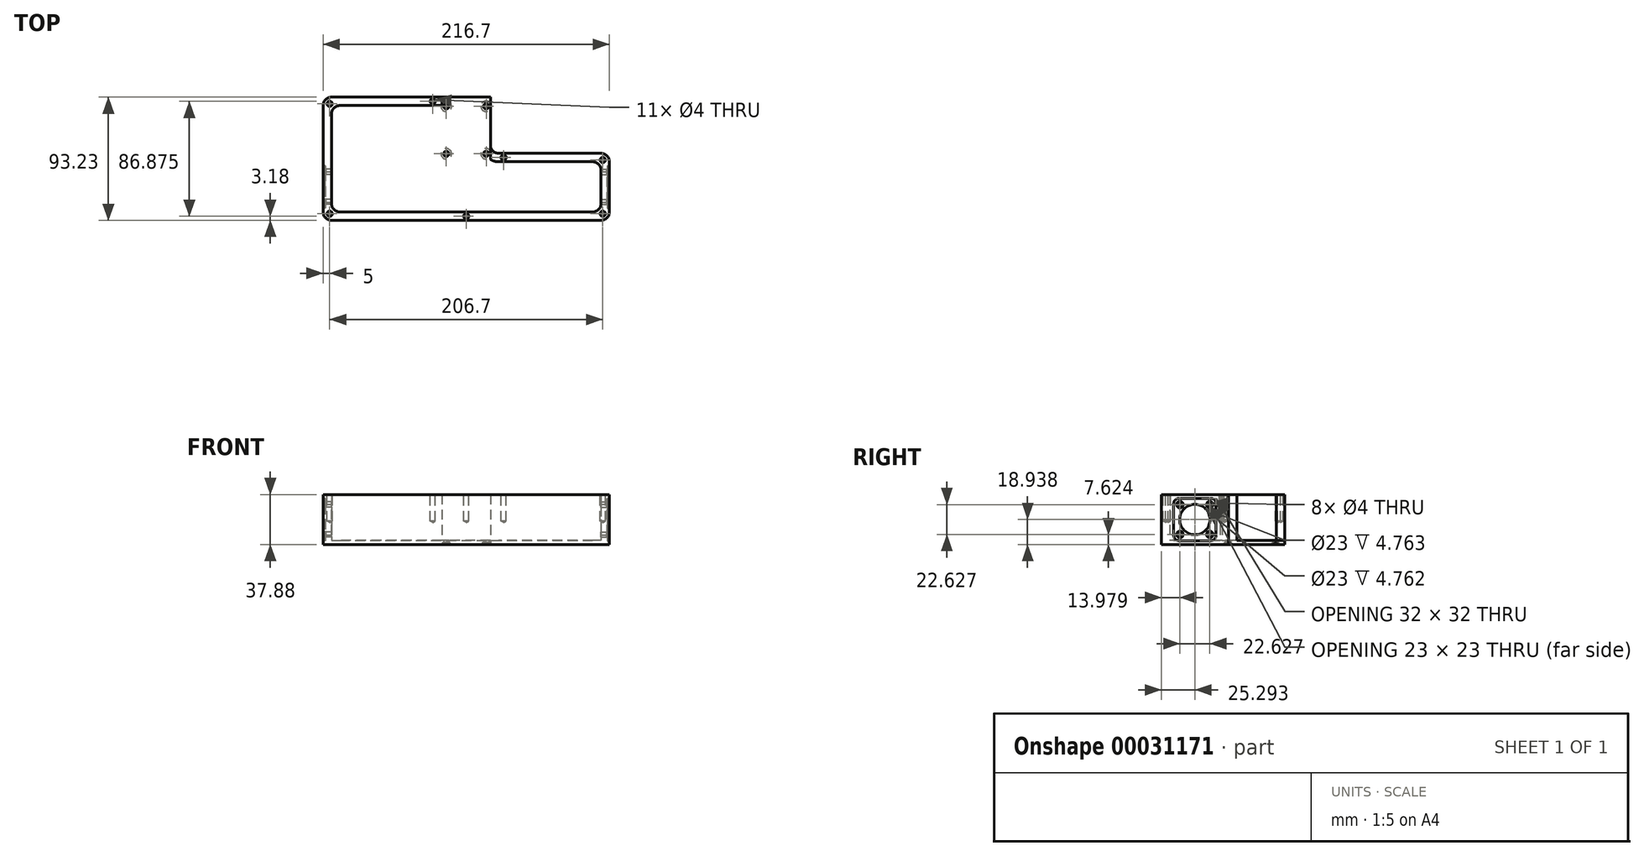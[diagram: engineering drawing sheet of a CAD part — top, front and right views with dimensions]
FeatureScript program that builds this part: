
annotation { "Feature Type Name" : "Feature", "Feature Type Description" : "" }
export const myFeature = defineFeature(function(context is Context, id is Id, definition is map)
    precondition{}
    {
        {
            var Q0;
            Q0=qCreatedBy(makeId("Top.planeOp"),FACE);
            var sketch = newSketch(context, id + "F0", { "sketchPlane" : qUnion([Q0])});
            skLineSegment(sketch, "E0", {"start": v(0, 0) * mm, "end": v(0, -93.23) * mm});
            skLineSegment(sketch, "E1", {"start": v(0, -93.23) * mm, "end": v(216.7, -93.23) * mm});
            skLineSegment(sketch, "E2", {"start": v(216.7, -93.23) * mm, "end": v(216.7, -42.52) * mm});
            skLineSegment(sketch, "E3", {"start": v(216.7, -42.52) * mm, "end": v(126.61, -42.52) * mm});
            skLineSegment(sketch, "E4", {"start": v(126.61, -42.52) * mm, "end": v(126.61, 0) * mm});
            skLineSegment(sketch, "E5", {"start": v(126.61, 0) * mm, "end": v(90.09, 0) * mm});
            skLineSegment(sketch, "E6", {"start": v(90.09, 0) * mm, "end": v(90.09, -93.23) * mm, "construction": true});
            skLineSegment(sketch, "E7", {"start": v(90.09, 0) * mm, "end": v(0, 0) * mm});
            skSolve(sketch);
        }
        {
            var Q0;
            Q0 = qSketchRegion(id + "F0", true);
            extrude(context, id + "F1", {"entities" : qUnion([Q0]), "depth" : 3.17 * mm});
        }
        {
            var Q0;
            Q0=makeQuery(id+"F1.opExtrude","SWEPT_EDGE",EDGE,{"disambiguationData":[OSD([sQuery(id+"F0.wireOp",EDGE,"E3"),sQuery(id+"F0.wireOp",EDGE,"E4")])]});
            fillet(context, id + "F2", {"entities" : qUnion([Q0]), "radius" : 6.35 * mm, "tangentPropagation" : true, "allowEdgeOverflow" : false});
        }
        {
            var Q0;
            Q0=makeQuery(id+"F1.opExtrude","SWEPT_EDGE",EDGE,{"disambiguationData":[OSD([sQuery(id+"F0.wireOp",EDGE,"E2"),sQuery(id+"F0.wireOp",EDGE,"E3")])]});
            var Q1;
            Q1=makeQuery(id+"F1.opExtrude","SWEPT_EDGE",EDGE,{"disambiguationData":[OSD([sQuery(id+"F0.wireOp",EDGE,"E1"),sQuery(id+"F0.wireOp",EDGE,"E2")])]});
            var Q2;
            Q2=makeQuery(id+"F1.opExtrude","SWEPT_EDGE",EDGE,{"disambiguationData":[OSD([sQuery(id+"F0.wireOp",EDGE,"E0"),sQuery(id+"F0.wireOp",EDGE,"E1")])]});
            var Q3;
            Q3=makeQuery(id+"F1.opExtrude","SWEPT_EDGE",EDGE,{"disambiguationData":[OSD([sQuery(id+"F0.wireOp",EDGE,"E0"),sQuery(id+"F0.wireOp",EDGE,"E7")])]});
            fillet(context, id + "F3", {"entities" : qUnion([Q0, Q1, Q2, Q3]), "radius" : 6.35 * mm, "tangentPropagation" : true, "allowEdgeOverflow" : false});
        }
        {
            var Q0;
            Q0=makeQuery(id+"F1.opExtrude","CAP_FACE",FACE,{"disambiguationData":[OSD([sQuery(id+"F0.wireOp",EDGE,"E0"),sQuery(id+"F0.wireOp",EDGE,"E1"),sQuery(id+"F0.wireOp",EDGE,"E2"),sQuery(id+"F0.wireOp",EDGE,"E3"),sQuery(id+"F0.wireOp",EDGE,"E4"),sQuery(id+"F0.wireOp",EDGE,"E5"),sQuery(id+"F0.wireOp",EDGE,"E7")])],"isStart":false});
            var sketch = newSketch(context, id + "F4", { "sketchPlane" : qUnion([Q0])});
            skArc(sketch, "E8.0", {"start": v(132.96, -48.88) * mm, "mid": v(129.68, -48.44) * mm, "end": v(126.61, -47.17) * mm});
            skLineSegment(sketch, "E8.1", {"start": v(204, -48.88) * mm, "end": v(132.96, -48.88) * mm});
            skLineSegment(sketch, "E8.2", {"start": v(90.09, -6.35) * mm, "end": v(12.7, -6.35) * mm});
            skLineSegment(sketch, "E8.3", {"start": v(6.35, -12.7) * mm, "end": v(6.35, -80.53) * mm});
            skLineSegment(sketch, "E8.4", {"start": v(12.7, -86.88) * mm, "end": v(204, -86.88) * mm});
            skLineSegment(sketch, "E8.5", {"start": v(210.35, -80.53) * mm, "end": v(210.35, -55.23) * mm});
            skPoint(sketch, "E9.visualSharp", {"position": v(6.35, -6.35) * mm});
            skArc(sketch, "E9.filletArc", {"start": v(12.7, -6.35) * mm, "mid": v(8.2, -8.2) * mm, "end": v(6.35, -12.7) * mm});
            skPoint(sketch, "E10.visualSharp", {"position": v(6.35, -86.88) * mm});
            skArc(sketch, "E10.filletArc", {"start": v(6.35, -80.53) * mm, "mid": v(8.2, -85.02) * mm, "end": v(12.7, -86.88) * mm});
            skPoint(sketch, "E11.visualSharp", {"position": v(210.35, -86.88) * mm});
            skArc(sketch, "E11.filletArc", {"start": v(204, -86.88) * mm, "mid": v(208.5, -85.02) * mm, "end": v(210.35, -80.53) * mm});
            skPoint(sketch, "E12.visualSharp", {"position": v(210.35, -48.88) * mm});
            skArc(sketch, "E12.filletArc", {"start": v(210.35, -55.23) * mm, "mid": v(208.5, -50.73) * mm, "end": v(204, -48.88) * mm});
            skLineSegment(sketch, "E13", {"start": v(90.09, -6.35) * mm, "end": v(90.09, 0) * mm});
            skLineSegment(sketch, "E14", {"start": v(126.61, -47.17) * mm, "end": v(126.61, -36.17) * mm});
            skLineSegment(sketch, "E15", {"start": v(90.09, 0) * mm, "end": v(6.35, 0) * mm});
            skLineSegment(sketch, "E16", {"start": v(0, -6.35) * mm, "end": v(0, -86.88) * mm});
            skLineSegment(sketch, "E17", {"start": v(6.35, -93.23) * mm, "end": v(210.35, -93.23) * mm});
            skLineSegment(sketch, "E18", {"start": v(216.7, -86.88) * mm, "end": v(216.7, -48.88) * mm});
            skLineSegment(sketch, "E19", {"start": v(210.35, -42.52) * mm, "end": v(132.96, -42.53) * mm});
            skArc(sketch, "E20", {"start": v(6.35, 0) * mm, "mid": v(1.86, -1.86) * mm, "end": v(0, -6.35) * mm});
            skArc(sketch, "E21", {"start": v(0, -86.88) * mm, "mid": v(1.86, -91.37) * mm, "end": v(6.35, -93.23) * mm});
            skArc(sketch, "E22", {"start": v(210.35, -93.22) * mm, "mid": v(214.84, -91.37) * mm, "end": v(216.7, -86.88) * mm});
            skArc(sketch, "E23", {"start": v(216.7, -48.88) * mm, "mid": v(214.84, -44.38) * mm, "end": v(210.35, -42.52) * mm});
            skArc(sketch, "E24", {"start": v(126.61, -36.17) * mm, "mid": v(128.47, -40.67) * mm, "end": v(132.96, -42.53) * mm});
            skSolve(sketch);
        }
        {
            var Q0;
            Q0 = qSketchRegion(id + "F4", true);
            extrude(context, id + "F5", {"entities" : qUnion([Q0]), "operationType" : NewBodyOperationType.ADD, "depth" : 34.7 * mm});
        }
        {
            var Q0;
            Q0=makeQuery(id+"F5.boolean.opBoolean","MERGE",FACE,{"derivedFrom":[makeQuery(id+"F1.opExtrude","SWEPT_FACE",FACE,{"disambiguationData":[OSD([sQuery(id+"F0.wireOp",EDGE,"E2")])]}),makeQuery(id+"F5.opExtrude","SWEPT_FACE",FACE,{"disambiguationData":[OSD([sQuery(id+"F4.wireOp",EDGE,"E18")])]})]});
            var sketch = newSketch(context, id + "F6", { "sketchPlane" : qUnion([Q0])});
            skLineSegment(sketch, "E25.rect.bottom", {"start": v(-55.94, 34.94) * mm, "end": v(-79.94, 34.94) * mm});
            skLineSegment(sketch, "E25.rect.top", {"start": v(-55.94, 2.94) * mm, "end": v(-79.94, 2.94) * mm});
            skLineSegment(sketch, "E25.rect.left", {"start": v(-51.94, 30.94) * mm, "end": v(-51.94, 6.94) * mm});
            skLineSegment(sketch, "E25.rect.right", {"start": v(-83.94, 30.94) * mm, "end": v(-83.94, 6.94) * mm});
            skPoint(sketch, "E25.rect.middle", {"position": v(-67.94, 18.94) * mm});
            skLineSegment(sketch, "E26", {"start": v(-83.94, 34.94) * mm, "end": v(-86.88, 34.94) * mm, "construction": true});
            skLineSegment(sketch, "E27", {"start": v(-83.94, 34.94) * mm, "end": v(-83.94, 37.88) * mm, "construction": true});
            skLineSegment(sketch, "E28", {"start": v(-83.94, 2.94) * mm, "end": v(-83.94, 0) * mm, "construction": true});
            skPoint(sketch, "E29.visualSharp", {"position": v(-83.94, 34.94) * mm});
            skArc(sketch, "E29.filletArc", {"start": v(-79.94, 34.94) * mm, "mid": v(-82.77, 33.77) * mm, "end": v(-83.94, 30.94) * mm});
            skPoint(sketch, "E30.visualSharp", {"position": v(-51.94, 34.94) * mm});
            skArc(sketch, "E30.filletArc", {"start": v(-51.94, 30.94) * mm, "mid": v(-53.1, 33.77) * mm, "end": v(-55.94, 34.94) * mm});
            skPoint(sketch, "E31.visualSharp", {"position": v(-51.94, 2.94) * mm});
            skArc(sketch, "E31.filletArc", {"start": v(-55.94, 2.94) * mm, "mid": v(-53.1, 4.1) * mm, "end": v(-51.94, 6.94) * mm});
            skPoint(sketch, "E32.visualSharp", {"position": v(-83.94, 2.94) * mm});
            skArc(sketch, "E32.filletArc", {"start": v(-83.94, 6.94) * mm, "mid": v(-82.77, 4.1) * mm, "end": v(-79.94, 2.94) * mm});
            skSolve(sketch);
        }
        {
            var Q0;
            Q0 = qSketchRegion(id + "F6", true);
            extrude(context, id + "F7", {"entities" : qUnion([Q0]), "operationType" : NewBodyOperationType.REMOVE, "oppositeDirection" : true, "depth" : 1.59 * mm});
        }
        {
            var Q0;
            Q0=makeQuery(id+"F7.boolean.opBoolean","COPY",FACE,{"derivedFrom":makeQuery(id+"F7.opExtrude","CAP_FACE",FACE,{"disambiguationData":[OSD([sQuery(id+"F6.wireOp",EDGE,"E25.rect.bottom"),sQuery(id+"F6.wireOp",EDGE,"E25.rect.top"),sQuery(id+"F6.wireOp",EDGE,"E25.rect.left"),sQuery(id+"F6.wireOp",EDGE,"E25.rect.right"),sQuery(id+"F6.wireOp",EDGE,"E29.filletArc"),sQuery(id+"F6.wireOp",EDGE,"E30.filletArc"),sQuery(id+"F6.wireOp",EDGE,"E31.filletArc"),sQuery(id+"F6.wireOp",EDGE,"E32.filletArc")])],"isStart":false})});
            var sketch = newSketch(context, id + "F8", { "sketchPlane" : qUnion([Q0])});
            skCircle(sketch, "E33", {"center": v(-67.94, 18.94) * mm, "radius": 11.5 * mm});
            skLineSegment(sketch, "E34", {"start": v(-67.94, 34.94) * mm, "end": v(-67.94, 2.94) * mm, "construction": true});
            skSolve(sketch);
        }
        {
            var Q0;
            Q0 = qSketchRegion(id + "F8", true);
            extrude(context, id + "F9", {"entities" : qUnion([Q0]), "operationType" : NewBodyOperationType.REMOVE, "endBound" : BoundingType.THROUGH_ALL, "oppositeDirection" : true, "depth" : 25 * mm});
        }
        {
            var Q0;
            Q0=makeQuery(id+"F5.boolean.opBoolean","MERGE",FACE,{"derivedFrom":[makeQuery(id+"F1.opExtrude","SWEPT_FACE",FACE,{"disambiguationData":[OSD([sQuery(id+"F0.wireOp",EDGE,"E2")])]}),makeQuery(id+"F5.opExtrude","SWEPT_FACE",FACE,{"disambiguationData":[OSD([sQuery(id+"F4.wireOp",EDGE,"E18")])]})]});
            var sketch = newSketch(context, id + "F10", { "sketchPlane" : qUnion([Q0])});
            skCircle(sketch, "E35", {"center": v(-67.94, 18.94) * mm, "radius": 16 * mm});
            skPoint(sketch, "E36", {"position": v(-79.25, 30.25) * mm});
            skPoint(sketch, "E37", {"position": v(-56.62, 30.25) * mm});
            skPoint(sketch, "E38", {"position": v(-56.62, 7.62) * mm});
            skPoint(sketch, "E39", {"position": v(-79.25, 7.62) * mm});
            skLineSegment(sketch, "E40.bottom", {"start": v(-79.25, 30.25) * mm, "end": v(-56.62, 30.25) * mm});
            skLineSegment(sketch, "E40.top", {"start": v(-79.25, 7.62) * mm, "end": v(-56.62, 7.62) * mm});
            skLineSegment(sketch, "E40.left", {"start": v(-79.25, 30.25) * mm, "end": v(-79.25, 7.62) * mm});
            skLineSegment(sketch, "E40.right", {"start": v(-56.62, 30.25) * mm, "end": v(-56.62, 7.62) * mm});
            skSolve(sketch);
        }
        {
            var Q0;
            Q0=sQuery(id+"F10.wireOp",VERTEX,"E36");
            var Q1;
            Q1=sQuery(id+"F10.wireOp",VERTEX,"E37");
            var Q2;
            Q2=sQuery(id+"F10.wireOp",VERTEX,"E38");
            var Q3;
            Q3=sQuery(id+"F10.wireOp",VERTEX,"E39");
            var Q4;
            Q4=makeQuery(id+"F1.opExtrude","SWEPT_BODY",BODY,{"disambiguationData":[OSD([sQuery(id+"F0.wireOp",EDGE,"E0"),sQuery(id+"F0.wireOp",EDGE,"E1"),sQuery(id+"F0.wireOp",EDGE,"E2"),sQuery(id+"F0.wireOp",EDGE,"E3"),sQuery(id+"F0.wireOp",EDGE,"E4"),sQuery(id+"F0.wireOp",EDGE,"E5"),sQuery(id+"F0.wireOp",EDGE,"E7")])]});
            hole(context, id + "F11", {"style" : HoleStyle.C_SINK, "holeDiameter" : 4 * mm, "cSinkDiameter" : 5 * mm, "endStyle" : HoleEndStyle.BLIND, "holeDepth" : 20 * mm, "locations" : qUnion([Q0, Q1, Q2, Q3]), "scope" : qUnion([Q4]), "cSinkAngle" : 90 * degree});
        }
        {
            var Q0;
            Q0=makeQuery(id+"F5.boolean.opBoolean","MERGE",FACE,{"derivedFrom":[makeQuery(id+"F1.opExtrude","SWEPT_FACE",FACE,{"disambiguationData":[OSD([sQuery(id+"F0.wireOp",EDGE,"E0")])]}),makeQuery(id+"F5.opExtrude","SWEPT_FACE",FACE,{"disambiguationData":[OSD([sQuery(id+"F4.wireOp",EDGE,"E16")])]})]});
            var sketch = newSketch(context, id + "F12", { "sketchPlane" : qUnion([Q0])});
            skLineSegment(sketch, "E41.bottom", {"start": v(55.94, 34.94) * mm, "end": v(79.94, 34.94) * mm});
            skLineSegment(sketch, "E41.top", {"start": v(55.94, 2.94) * mm, "end": v(79.94, 2.94) * mm});
            skLineSegment(sketch, "E41.left", {"start": v(51.94, 30.94) * mm, "end": v(51.94, 6.94) * mm});
            skLineSegment(sketch, "E41.right", {"start": v(83.94, 30.94) * mm, "end": v(83.94, 6.94) * mm});
            skLineSegment(sketch, "E42", {"start": v(83.94, 34.94) * mm, "end": v(83.94, 37.87) * mm, "construction": true});
            skLineSegment(sketch, "E43", {"start": v(83.94, 34.94) * mm, "end": v(86.88, 34.94) * mm, "construction": true});
            skLineSegment(sketch, "E44", {"start": v(83.94, 2.94) * mm, "end": v(83.94, 0) * mm, "construction": true});
            skPoint(sketch, "E45.visualSharp", {"position": v(51.94, 34.94) * mm});
            skArc(sketch, "E45.filletArc", {"start": v(55.94, 34.94) * mm, "mid": v(53.1, 33.77) * mm, "end": v(51.94, 30.94) * mm});
            skPoint(sketch, "E46.visualSharp", {"position": v(51.94, 2.94) * mm});
            skArc(sketch, "E46.filletArc", {"start": v(51.94, 6.94) * mm, "mid": v(53.1, 4.1) * mm, "end": v(55.94, 2.94) * mm});
            skPoint(sketch, "E47.visualSharp", {"position": v(83.94, 2.94) * mm});
            skArc(sketch, "E47.filletArc", {"start": v(79.94, 2.94) * mm, "mid": v(82.77, 4.1) * mm, "end": v(83.94, 6.94) * mm});
            skPoint(sketch, "E48.visualSharp", {"position": v(83.94, 34.94) * mm});
            skArc(sketch, "E48.filletArc", {"start": v(83.94, 30.94) * mm, "mid": v(82.77, 33.77) * mm, "end": v(79.94, 34.94) * mm});
            skSolve(sketch);
        }
        {
            var Q0;
            Q0 = qSketchRegion(id + "F12", true);
            extrude(context, id + "F13", {"entities" : qUnion([Q0]), "operationType" : NewBodyOperationType.REMOVE, "oppositeDirection" : true, "depth" : 1.59 * mm});
        }
        {
            var Q0;
            Q0=makeQuery(id+"F5.boolean.opBoolean","MERGE",FACE,{"derivedFrom":[makeQuery(id+"F1.opExtrude","SWEPT_FACE",FACE,{"disambiguationData":[OSD([sQuery(id+"F0.wireOp",EDGE,"E0")])]}),makeQuery(id+"F5.opExtrude","SWEPT_FACE",FACE,{"disambiguationData":[OSD([sQuery(id+"F4.wireOp",EDGE,"E16")])]})]});
            var sketch = newSketch(context, id + "F14", { "sketchPlane" : qUnion([Q0])});
            skCircle(sketch, "E49", {"center": v(67.94, 18.94) * mm, "radius": 16 * mm});
            skLineSegment(sketch, "E50.rect.bottom", {"start": v(79.25, 30.25) * mm, "end": v(56.62, 30.25) * mm});
            skLineSegment(sketch, "E50.rect.top", {"start": v(79.25, 7.62) * mm, "end": v(56.62, 7.62) * mm});
            skLineSegment(sketch, "E50.rect.left", {"start": v(79.25, 30.25) * mm, "end": v(79.25, 7.62) * mm});
            skLineSegment(sketch, "E50.rect.right", {"start": v(56.62, 30.25) * mm, "end": v(56.62, 7.62) * mm});
            skPoint(sketch, "E51", {"position": v(56.62, 30.25) * mm});
            skPoint(sketch, "E52", {"position": v(56.62, 7.62) * mm});
            skPoint(sketch, "E53", {"position": v(79.25, 7.62) * mm});
            skPoint(sketch, "E54", {"position": v(79.25, 30.25) * mm});
            skSolve(sketch);
        }
        {
            var Q0;
            Q0=sQuery(id+"F14.wireOp",VERTEX,"E51");
            var Q1;
            Q1=sQuery(id+"F14.wireOp",VERTEX,"E52");
            var Q2;
            Q2=sQuery(id+"F14.wireOp",VERTEX,"E53");
            var Q3;
            Q3=sQuery(id+"F14.wireOp",VERTEX,"E54");
            var Q4;
            Q4=makeQuery(id+"F1.opExtrude","SWEPT_BODY",BODY,{"disambiguationData":[OSD([sQuery(id+"F0.wireOp",EDGE,"E0"),sQuery(id+"F0.wireOp",EDGE,"E1"),sQuery(id+"F0.wireOp",EDGE,"E2"),sQuery(id+"F0.wireOp",EDGE,"E3"),sQuery(id+"F0.wireOp",EDGE,"E4"),sQuery(id+"F0.wireOp",EDGE,"E5"),sQuery(id+"F0.wireOp",EDGE,"E7")])]});
            hole(context, id + "F15", {"style" : HoleStyle.C_SINK, "holeDiameter" : 4 * mm, "cSinkDiameter" : 5 * mm, "endStyle" : HoleEndStyle.BLIND, "holeDepth" : 20 * mm, "locations" : qUnion([Q0, Q1, Q2, Q3]), "scope" : qUnion([Q4]), "cSinkAngle" : 90 * degree});
        }
        {
            var Q0;
            Q0=makeQuery(id+"F5.opExtrude","CAP_FACE",FACE,{"disambiguationData":[OSD([sQuery(id+"F4.wireOp",EDGE,"E8.0"),sQuery(id+"F4.wireOp",EDGE,"E8.1"),sQuery(id+"F4.wireOp",EDGE,"E8.2"),sQuery(id+"F4.wireOp",EDGE,"E8.3"),sQuery(id+"F4.wireOp",EDGE,"E8.4"),sQuery(id+"F4.wireOp",EDGE,"E8.5"),sQuery(id+"F4.wireOp",EDGE,"E9.filletArc"),sQuery(id+"F4.wireOp",EDGE,"E10.filletArc"),sQuery(id+"F4.wireOp",EDGE,"E11.filletArc"),sQuery(id+"F4.wireOp",EDGE,"E12.filletArc"),sQuery(id+"F4.wireOp",EDGE,"E13"),sQuery(id+"F4.wireOp",EDGE,"E14"),sQuery(id+"F4.wireOp",EDGE,"E15"),sQuery(id+"F4.wireOp",EDGE,"E16"),sQuery(id+"F4.wireOp",EDGE,"E17"),sQuery(id+"F4.wireOp",EDGE,"E18"),sQuery(id+"F4.wireOp",EDGE,"E19"),sQuery(id+"F4.wireOp",EDGE,"E20"),sQuery(id+"F4.wireOp",EDGE,"E21"),sQuery(id+"F4.wireOp",EDGE,"E22"),sQuery(id+"F4.wireOp",EDGE,"E23"),sQuery(id+"F4.wireOp",EDGE,"E24")])],"isStart":false});
            var sketch = newSketch(context, id + "F16", { "sketchPlane" : qUnion([Q0])});
            skPoint(sketch, "E55", {"position": v(5, -5) * mm});
            skPoint(sketch, "E56", {"position": v(5, -88.22) * mm});
            skPoint(sketch, "E57", {"position": v(211.7, -88.22) * mm});
            skPoint(sketch, "E58", {"position": v(211.7, -47.52) * mm});
            skPoint(sketch, "E59", {"position": v(136.61, -45.7) * mm});
            skPoint(sketch, "E60", {"position": v(83, -3.17) * mm});
            skPoint(sketch, "E61", {"position": v(108.35, -90.05) * mm});
            skPoint(sketch, "E61.positionSnap0", {"position": v(108.35, -93.23) * mm});
            skSolve(sketch);
        }
        {
            var Q0;
            Q0=sQuery(id+"F16.wireOp",VERTEX,"E55");
            var Q1;
            Q1=sQuery(id+"F16.wireOp",VERTEX,"E56");
            var Q2;
            Q2=sQuery(id+"F16.wireOp",VERTEX,"E57");
            var Q3;
            Q3=sQuery(id+"F16.wireOp",VERTEX,"E58");
            var Q4;
            Q4=sQuery(id+"F16.wireOp",VERTEX,"E59");
            var Q5;
            Q5=sQuery(id+"F16.wireOp",VERTEX,"E60");
            var Q6;
            Q6=sQuery(id+"F16.wireOp",VERTEX,"E61");
            var Q7;
            Q7=makeQuery(id+"F1.opExtrude","SWEPT_BODY",BODY,{"disambiguationData":[OSD([sQuery(id+"F0.wireOp",EDGE,"E0"),sQuery(id+"F0.wireOp",EDGE,"E1"),sQuery(id+"F0.wireOp",EDGE,"E2"),sQuery(id+"F0.wireOp",EDGE,"E3"),sQuery(id+"F0.wireOp",EDGE,"E4"),sQuery(id+"F0.wireOp",EDGE,"E5"),sQuery(id+"F0.wireOp",EDGE,"E7")])]});
            hole(context, id + "F17", {"style" : HoleStyle.SIMPLE, "holeDiameter" : 4 * mm, "endStyle" : HoleEndStyle.BLIND, "holeDepth" : 20 * mm, "locations" : qUnion([Q0, Q1, Q2, Q3, Q4, Q5, Q6]), "scope" : qUnion([Q7])});
        }
        {
            var Q0;
            Q0=makeQuery(id+"F1.opExtrude","CAP_FACE",FACE,{"disambiguationData":[OSD([sQuery(id+"F0.wireOp",EDGE,"E0"),sQuery(id+"F0.wireOp",EDGE,"E1"),sQuery(id+"F0.wireOp",EDGE,"E2"),sQuery(id+"F0.wireOp",EDGE,"E3"),sQuery(id+"F0.wireOp",EDGE,"E4"),sQuery(id+"F0.wireOp",EDGE,"E5"),sQuery(id+"F0.wireOp",EDGE,"E7")])],"isStart":false});
            var sketch = newSketch(context, id + "F18", { "sketchPlane" : qUnion([Q0])});
            skLineSegment(sketch, "E62", {"start": v(93.26, 0) * mm, "end": v(93.26, -48.87) * mm, "construction": true});
            skPoint(sketch, "E63", {"position": v(93.26, -42.88) * mm});
            skPoint(sketch, "E64", {"position": v(93.26, -6.87) * mm});
            skLineSegment(sketch, "E65", {"start": v(123.44, 0) * mm, "end": v(123.44, -48.87) * mm, "construction": true});
            skPoint(sketch, "E66", {"position": v(123.44, -42.88) * mm});
            skPoint(sketch, "E67", {"position": v(123.44, -6.87) * mm});
            skSolve(sketch);
        }
        {
            var Q0;
            Q0=makeQuery(id+"F1.opExtrude","CAP_FACE",FACE,{"disambiguationData":[OSD([sQuery(id+"F0.wireOp",EDGE,"E0"),sQuery(id+"F0.wireOp",EDGE,"E1"),sQuery(id+"F0.wireOp",EDGE,"E2"),sQuery(id+"F0.wireOp",EDGE,"E3"),sQuery(id+"F0.wireOp",EDGE,"E4"),sQuery(id+"F0.wireOp",EDGE,"E5"),sQuery(id+"F0.wireOp",EDGE,"E7")])],"isStart":true});
            var sketch = newSketch(context, id + "F19", { "sketchPlane" : qUnion([Q0])});
            skLineSegment(sketch, "E68", {"start": v(93.26, 48.87) * mm, "end": v(93.26, 0) * mm, "construction": true});
            skPoint(sketch, "E69", {"position": v(93.26, 6.87) * mm});
            skPoint(sketch, "E70", {"position": v(93.26, 42.88) * mm});
            skLineSegment(sketch, "E71", {"start": v(123.44, 52.76) * mm, "end": v(123.44, 0) * mm, "construction": true});
            skPoint(sketch, "E72", {"position": v(123.44, 6.87) * mm});
            skPoint(sketch, "E73", {"position": v(123.44, 42.88) * mm});
            skSolve(sketch);
        }
        {
            var Q0;
            Q0=sQuery(id+"F19.wireOp",VERTEX,"E72");
            var Q1;
            Q1=sQuery(id+"F19.wireOp",VERTEX,"E73");
            var Q2;
            Q2=sQuery(id+"F19.wireOp",VERTEX,"E70");
            var Q3;
            Q3=sQuery(id+"F19.wireOp",VERTEX,"E69");
            var Q4;
            Q4=makeQuery(id+"F1.opExtrude","SWEPT_BODY",BODY,{"disambiguationData":[OSD([sQuery(id+"F0.wireOp",EDGE,"E0"),sQuery(id+"F0.wireOp",EDGE,"E1"),sQuery(id+"F0.wireOp",EDGE,"E2"),sQuery(id+"F0.wireOp",EDGE,"E3"),sQuery(id+"F0.wireOp",EDGE,"E4"),sQuery(id+"F0.wireOp",EDGE,"E5"),sQuery(id+"F0.wireOp",EDGE,"E7")])]});
            hole(context, id + "F20", {"style" : HoleStyle.C_SINK, "holeDiameter" : 4 * mm, "cSinkDiameter" : 8 * mm, "endStyle" : HoleEndStyle.THROUGH, "locations" : qUnion([Q0, Q1, Q2, Q3]), "scope" : qUnion([Q4]), "cSinkAngle" : 90 * degree});
        }
    });
